# Revit family: ACLE_04L_LE
name_source: partatom
category: Lighting Fixtures
revit_build: Autodesk Revit 2014 (Build: 20130308_1515(x64)
units: mm (PartAtom-declared; Revit-internal decimal feet)

## types (1)
- ACLE_04L_LE
    Apparent Load = 40 VA
    Assembly Code = D5020200
    Color Filter = 16777215
    Connector Description = Lighting Connector
    Default Elevation = 1219.2 mm  [stored 4 ft]
    Description = Acclaim Recessible Luminaire is designed for use in offshore accommodation areas and control rooms where it provides recessible and escape lighting. Manufactured from zinc coated sheet steel the luminaire is suitable for installation in fire resistant ceilings up to solas B15 rating. The mounting and cover details are flexible to allow luminaires to be recessed into a variety of ceiling types.
    Dimming Lamp Color Temperature Shift = <None>
    Drum-Height = 609.6 mm  [stored 2 ft]
    Emit Shape Visible in Rendering = No
    Emit from Rectangle Length = 300 mm
    Emit from Rectangle Width = 1365 mm  [stored 4.47835 ft]
    Features = Automatic lamp de-energisation
on opening
Battery management, monitoring
and automatic self test
Resistant to voltage fluctuations
Local switching arrangement
as standard
Ingress protection to IP65
dc operation (non emergency)
B15 SOLAS fire rating - appropriate
insulation is required over the luminaire
Emergency inhibition and power
off re-start
End of life (EOL) protection
to IEC 60079-7
(with EOL I and EOL II functionality
    Fixture distribution = Direct
    Housing Material = Paint - Hubbell - Matte White
    IP Rating = IP65
    Lamp = LED
    Length = 1365 mm  [stored 4.47835 ft]
    Load Classification = Lighting
    Manufacturer = Chalmit
    Model = ACLE_04L_LE
    Mounting = Paint - Hubbell - Light Silver
    Photometric Web File = ACLE_04L_LE.ies
    Power Factor = 1
    Product Documentation Link = https://hubbellcdn.com
    Product Link = https://www.hubbell.com
    Reflector Finish = Hubbell - White Glass
    Tilt Angle = 90.00°
    URL = https://www.hubbell.com
    Voltage = 120 V
    Warranty = 5 years Warranty
    Wattage Comments = 40W
    Watts = 40 W
    Width = 309 mm  [stored 1.01378 ft]
    Wings = Paint - Hubbell - Light Silver

note: [stored X ft] marks values corroborated as IEEE doubles in the binary element streams (Revit-internal decimal feet)

## geometry (parser evidence)
native form markers: Sweep x4
no freeform markers — native parametric forms only
